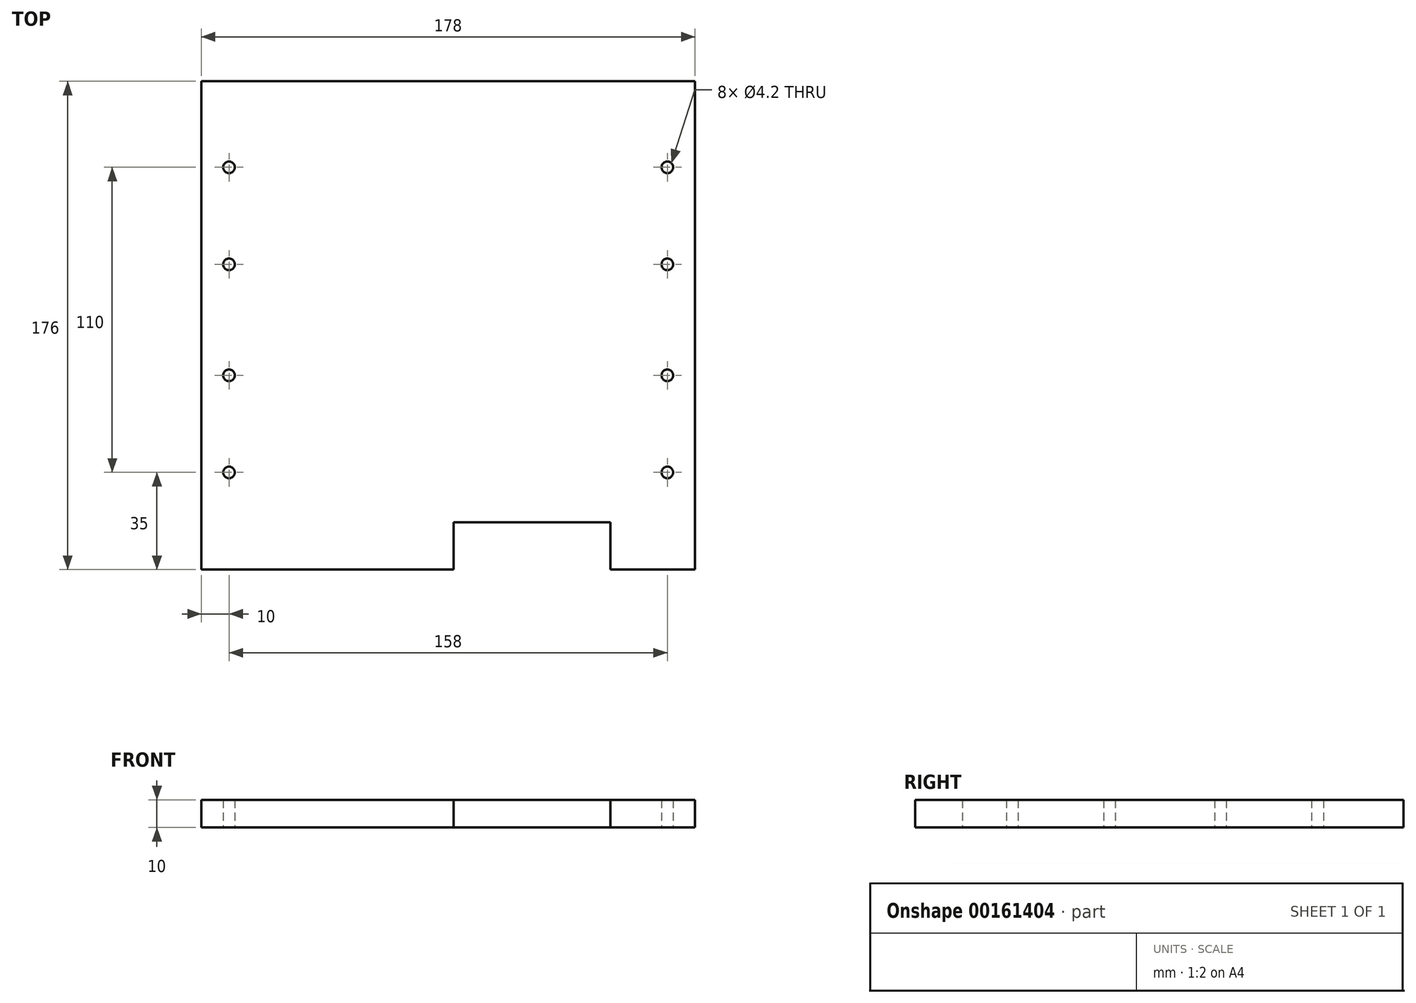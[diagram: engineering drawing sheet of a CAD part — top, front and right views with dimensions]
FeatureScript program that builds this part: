
annotation { "Feature Type Name" : "Feature", "Feature Type Description" : "" }
export const myFeature = defineFeature(function(context is Context, id is Id, definition is map)
    precondition{}
    {
        {
            var Q0;
            Q0=qCreatedBy(makeId("Top.planeOp"),FACE);
            var sketch = newSketch(context, id + "F0", { "sketchPlane" : qUnion([Q0])});
            skLineSegment(sketch, "E0.bottom", {"start": v(89, 88) * mm, "end": v(-89, 88) * mm});
            skLineSegment(sketch, "E0.top", {"start": v(89, -88) * mm, "end": v(58.5, -88) * mm});
            skLineSegment(sketch, "E0.left", {"start": v(89, 88) * mm, "end": v(89, -88) * mm});
            skLineSegment(sketch, "E0.right", {"start": v(-89, 88) * mm, "end": v(-89, -88) * mm});
            skPoint(sketch, "E0.middle", {"position": v(0, 0) * mm});
            skLineSegment(sketch, "E1.top", {"start": v(58.5, -71) * mm, "end": v(2, -71) * mm});
            skLineSegment(sketch, "E1.left", {"start": v(58.5, -88) * mm, "end": v(58.5, -71) * mm});
            skLineSegment(sketch, "E1.right", {"start": v(2, -88) * mm, "end": v(2, -71) * mm});
            skLineSegment(sketch, "E2.trimOffspring", {"start": v(2, -88) * mm, "end": v(-89, -88) * mm});
            skPoint(sketch, "E3", {"position": v(79, -53) * mm});
            skPoint(sketch, "E4", {"position": v(79, -18) * mm});
            skPoint(sketch, "E5", {"position": v(79, 22) * mm});
            skPoint(sketch, "E6", {"position": v(79, 57) * mm});
            skPoint(sketch, "E7", {"position": v(-79, 57) * mm});
            skPoint(sketch, "E8", {"position": v(-79, 22) * mm});
            skPoint(sketch, "E9", {"position": v(-79, -18) * mm});
            skPoint(sketch, "E10", {"position": v(-79, -53) * mm});
            skCircle(sketch, "E11", {"center": v(-79, 57) * mm, "radius": 2.1 * mm});
            skCircle(sketch, "E12", {"center": v(-79, 22) * mm, "radius": 2.1 * mm});
            skCircle(sketch, "E13", {"center": v(-79, -18) * mm, "radius": 2.1 * mm});
            skCircle(sketch, "E14", {"center": v(-79, -53) * mm, "radius": 2.1 * mm});
            skCircle(sketch, "E15", {"center": v(79, -53) * mm, "radius": 2.1 * mm});
            skCircle(sketch, "E16", {"center": v(79, -18) * mm, "radius": 2.1 * mm});
            skCircle(sketch, "E17", {"center": v(79, 22) * mm, "radius": 2.1 * mm});
            skCircle(sketch, "E18", {"center": v(79, 57) * mm, "radius": 2.1 * mm});
            skSolve(sketch);
        }
        {
            var Q0;
            Q0 = qSketchRegion(id + "F0", true);
            extrude(context, id + "F1", {"entities" : qUnion([Q0]), "depth" : 10 * mm});
        }
    });
